# Revit family: Bed_Pan-American_Standard-Institutional-7582.167
name_source: partatom
category: Plumbing Fixtures
revit_build: Autodesk Revit 2018 (Build: 20170223_1515(x64)
units: mm (PartAtom-declared; Revit-internal decimal feet)

## family parameters
Cut with Voids When Loaded = No
Host = Face
OmniClass Number = 23.45.05.14.37
OmniClass Title = Bedpan Washers/Sanitizers
Part Type = Normal
Room Calculation Point = No
Round Connector Dimension = Use Diameter
Shared = Yes

## types (1)
- 7582167.002
    Assembly Code = D2020100
    CW Connection = Yes
    CWFU = 1.5
    Default Elevation = 0"
    Description = Bedpan Cleanser With Atmospheric Vacuum Breaker and Loose Key Stop
    Finish = Brass-American Standard-002-Polished Chrome
    Finish - Handle = Rubber-American Standard-Blue
    Finish - Hose = Rubber-American Standard-Yellow
    HW Connection = No
    HWFU = 1.5
    Height = 17 7/8"
    Height Finished Floor = 50"
    Hose Length = 45 5/8"
    Inlet Diameter Connection = 3/8"
    Length = 3 1/4"
    Manufacturer = American Standard
    Material = Brass-American Standard-002-Polished Chrome
    Model = 7582167.002
    Product Documentation Link = https://americanstandard.box.com
    Product Page URL = https://www.americanstandard-us.com
    Revised Date = 09/22/2021
    URL = https://www.americanstandard-us.com
    Vent Connection = No
    WFU = 2
    Waste Connection = No
    Width = 2 1/16"

## geometry (parser evidence)
native form markers: Sweep x2
no freeform markers — native parametric forms only
